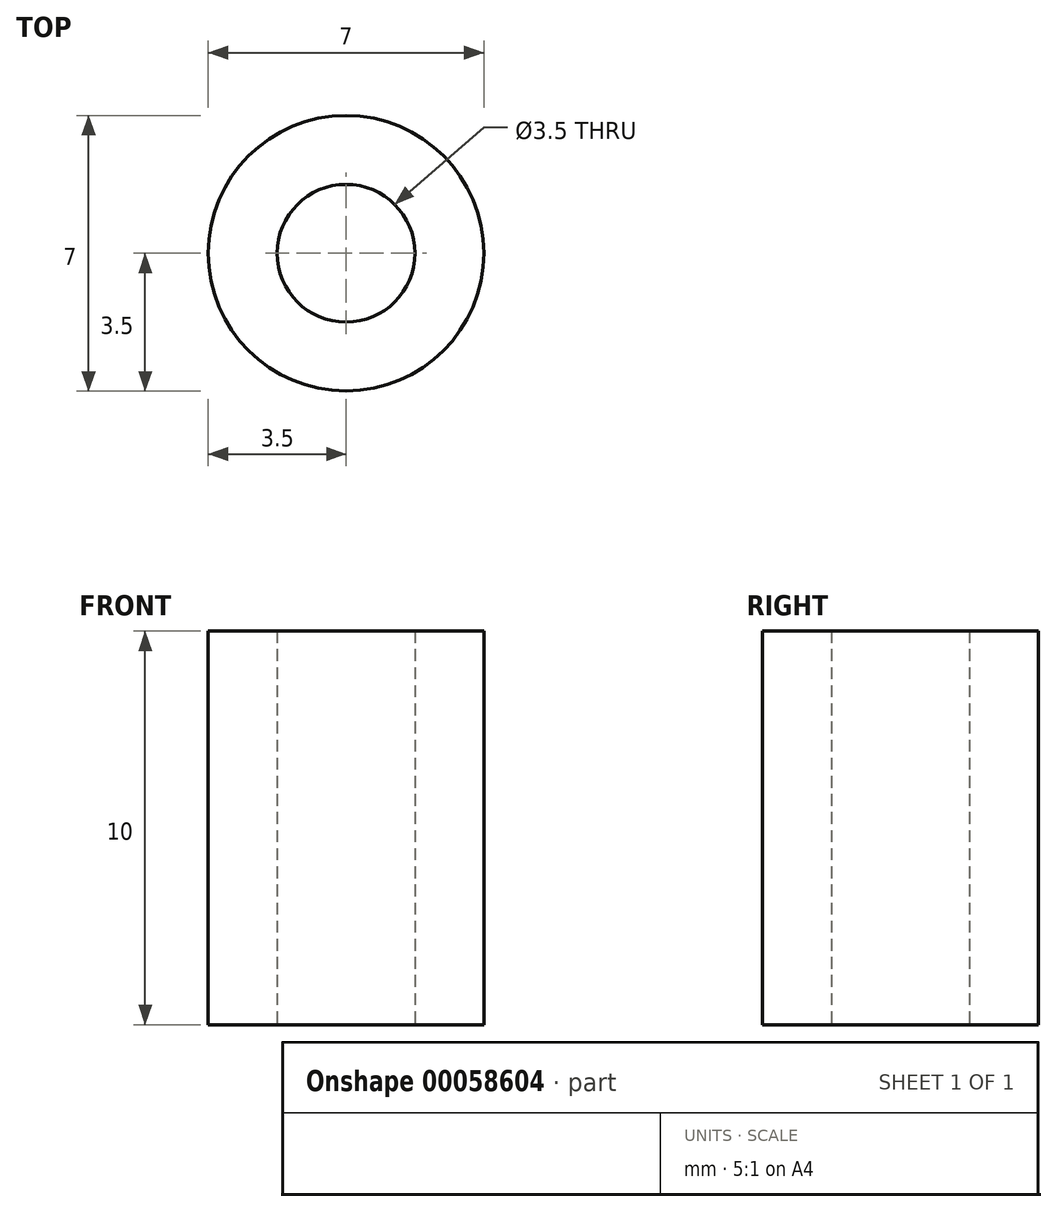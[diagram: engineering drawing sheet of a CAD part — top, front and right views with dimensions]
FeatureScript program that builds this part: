
annotation { "Feature Type Name" : "Feature", "Feature Type Description" : "" }
export const myFeature = defineFeature(function(context is Context, id is Id, definition is map)
    precondition{}
    {
        {
            var Q0;
            Q0=qCreatedBy(makeId("Top.planeOp"),FACE);
            var sketch = newSketch(context, id + "F0", { "sketchPlane" : qUnion([Q0])});
            skCircle(sketch, "E0", {"center": v(0, 0) * mm, "radius": 1.75 * mm});
            skCircle(sketch, "E1", {"center": v(0, 0) * mm, "radius": 3.5 * mm});
            skSolve(sketch);
        }
        {
            var Q0;
            Q0=makeQuery(id+"F0.imprint","IMPRINT",FACE,{"disambiguationData":[TD([[makeQuery(id+"F0.imprint","IMPRINT",EDGE,{"derivedFrom":sQuery(id+"F0.wireOp",EDGE,"E0")}),-1.0]])]});
            extrude(context, id + "F1", {"entities" : qUnion([Q0]), "depth" : 10 * mm});
        }
    });
